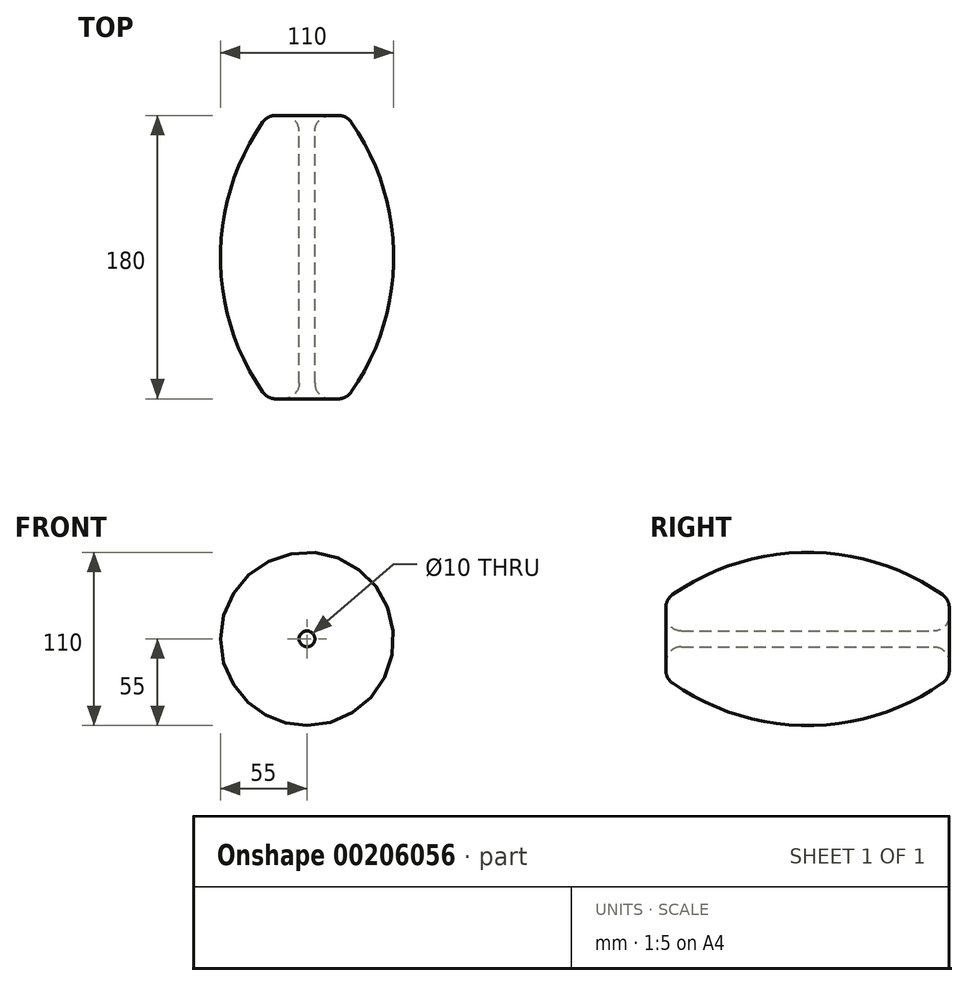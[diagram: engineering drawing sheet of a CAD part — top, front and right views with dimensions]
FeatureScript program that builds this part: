
annotation { "Feature Type Name" : "Feature", "Feature Type Description" : "" }
export const myFeature = defineFeature(function(context is Context, id is Id, definition is map)
    precondition{}
    {
        {
            var Q0;
            Q0=qCreatedBy(makeId("Right.planeOp"),FACE);
            var sketch = newSketch(context, id + "F0", { "sketchPlane" : qUnion([Q0])});
            skCircle(sketch, "E0", {"center": v(0, -95) * mm, "radius": 150 * mm});
            skLineSegment(sketch, "E1", {"start": v(90, 5) * mm, "end": v(-90, 5) * mm});
            skLineSegment(sketch, "E2", {"start": v(-90, 5) * mm, "end": v(-90, 25) * mm});
            skLineSegment(sketch, "E3", {"start": v(90, 5) * mm, "end": v(90, 25) * mm});
            skSolve(sketch);
        }
        {
            var Q0;
            Q0=qCreatedBy(makeId("Right.planeOp"),FACE);
            var sketch = newSketch(context, id + "F1", { "sketchPlane" : qUnion([Q0])});
            skLineSegment(sketch, "E4", {"start": v(0, 0) * mm, "end": v(-81.05, 0) * mm});
            skSolve(sketch);
        }
        {
            var Q0;
            Q0=makeQuery(id+"F0.imprint","IMPRINT",FACE,{"disambiguationData":[TD([[makeQuery(id+"F0.imprint","IMPRINT",EDGE,{"derivedFrom":sQuery(id+"F0.wireOp",EDGE,"E1")}),-1.0]])]});
            var Q1;
            Q1=sQuery(id+"F1.wireOp",EDGE,"E4");
            revolve(context, id + "F2", {"entities" : qUnion([Q0]), "axis" : qUnion([Q1]), "revolveType" : RevolveType.FULL});
        }
        {
            var Q0;
            Q0=makeQuery(id+"F2.opRevolve","SWEPT_FACE",FACE,{"disambiguationData":[OSD([sQuery(id+"F0.wireOp",EDGE,"E2")])]});
            var Q1;
            Q1=makeQuery(id+"F2.opRevolve","SWEPT_FACE",FACE,{"disambiguationData":[OSD([sQuery(id+"F0.wireOp",EDGE,"E3")])]});
            fillet(context, id + "F3", {"entities" : qUnion([Q0, Q1]), "radius" : 10 * mm, "tangentPropagation" : true, "allowEdgeOverflow" : false});
        }
    });
